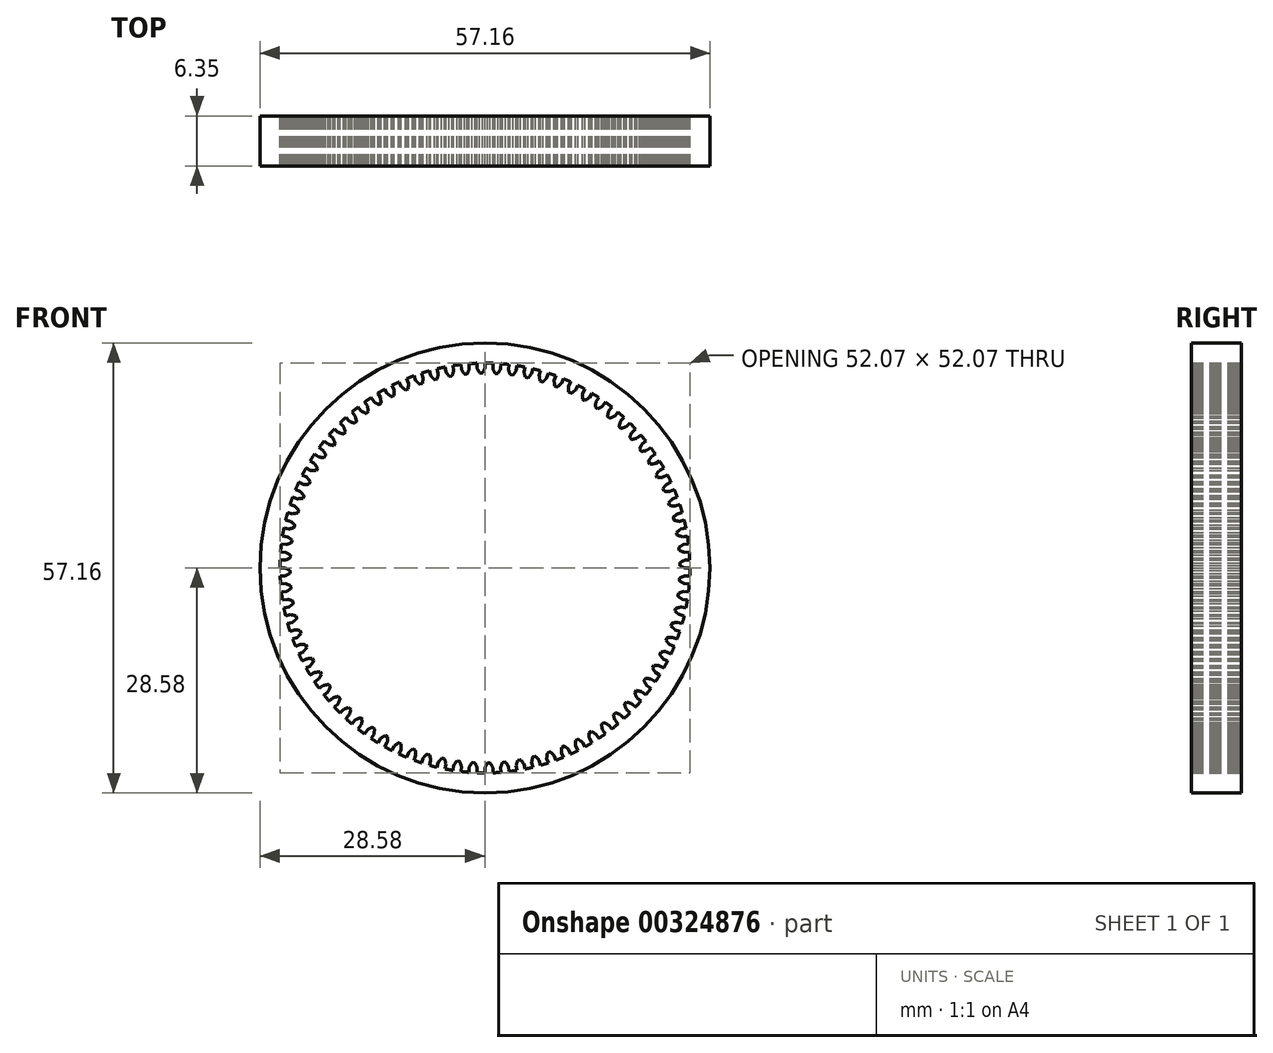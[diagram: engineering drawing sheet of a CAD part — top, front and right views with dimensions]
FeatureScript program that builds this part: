
annotation { "Feature Type Name" : "Feature", "Feature Type Description" : "" }
export const myFeature = defineFeature(function(context is Context, id is Id, definition is map)
    precondition{}
    {
        {
            var Q0;
            Q0=qCreatedBy(makeId("Front.planeOp"),FACE);
            var sketch = newSketch(context, id + "F0", { "sketchPlane" : qUnion([Q0])});
            skArc(sketch, "E0", {"start": v(-1.02, 26.01) * mm, "mid": v(-1.53, 25.99) * mm, "end": v(-2.04, 25.95) * mm});
            skArc(sketch, "E1.MirrorCS", {"start": v(0, 25.4) * mm, "mid": v(-0.14, 25.08) * mm, "end": v(-0.3, 24.77) * mm});
            skLineSegment(sketch, "E2.MirrorCS", {"start": v(0, 25.4) * mm, "end": v(0, 26.04) * mm});
            skLineSegment(sketch, "E3.MirrorCS", {"start": v(-1, 25.38) * mm, "end": v(-1.02, 26.01) * mm});
            skArc(sketch, "E4.MirrorCS", {"start": v(-1, 25.38) * mm, "mid": v(-0.84, 25.07) * mm, "end": v(-0.67, 24.76) * mm});
            skLineSegment(sketch, "E5", {"start": v(-0.67, 24.76) * mm, "end": v(-0.3, 24.77) * mm});
            skCircle(sketch, "E6", {"center": v(0, 0) * mm, "radius": 28.58 * mm});
            skLineSegment(sketch, "E7.1.0", {"start": v(-2, 25.32) * mm, "end": v(-2.04, 25.95) * mm});
            skLineSegment(sketch, "E7.1.1", {"start": v(-2.6, 24.63) * mm, "end": v(-2.25, 24.67) * mm});
            skArc(sketch, "E7.1.2", {"start": v(-2, 25.32) * mm, "mid": v(-2.11, 25) * mm, "end": v(-2.25, 24.67) * mm});
            skLineSegment(sketch, "E7.1.3", {"start": v(-2.99, 25.22) * mm, "end": v(-3.06, 25.85) * mm});
            skArc(sketch, "E7.1.4", {"start": v(-2.99, 25.22) * mm, "mid": v(-2.8, 24.92) * mm, "end": v(-2.6, 24.63) * mm});
            skArc(sketch, "E7.1.5", {"start": v(-2.99, 25.22) * mm, "mid": v(-2.8, 24.92) * mm, "end": v(-2.6, 24.63) * mm});
            skLineSegment(sketch, "E7.2.0", {"start": v(-3.97, 25.09) * mm, "end": v(-4.07, 25.71) * mm});
            skLineSegment(sketch, "E7.2.1", {"start": v(-4.53, 24.35) * mm, "end": v(-4.18, 24.41) * mm});
            skArc(sketch, "E7.2.2", {"start": v(-3.97, 25.09) * mm, "mid": v(-4.07, 24.75) * mm, "end": v(-4.18, 24.41) * mm});
            skLineSegment(sketch, "E7.2.3", {"start": v(-4.96, 24.91) * mm, "end": v(-5.08, 25.53) * mm});
            skArc(sketch, "E7.2.4", {"start": v(-4.96, 24.91) * mm, "mid": v(-4.75, 24.63) * mm, "end": v(-4.53, 24.35) * mm});
            skArc(sketch, "E7.2.5", {"start": v(-4.96, 24.91) * mm, "mid": v(-4.75, 24.63) * mm, "end": v(-4.53, 24.35) * mm});
            skLineSegment(sketch, "E8.3.3.0", {"start": v(-6.43, 23.92) * mm, "end": v(-6.08, 24.01) * mm});
            skArc(sketch, "E8.6.3.0", {"start": v(-5.93, 24.7) * mm, "mid": v(-6, 24.35) * mm, "end": v(-6.08, 24.01) * mm});
            skLineSegment(sketch, "E8.7.3.0", {"start": v(-5.93, 24.7) * mm, "end": v(-6.08, 25.32) * mm});
            skLineSegment(sketch, "E8.10.3.0", {"start": v(-6.9, 24.45) * mm, "end": v(-7.07, 25.06) * mm});
            skArc(sketch, "E8.13.3.0", {"start": v(-6.9, 24.45) * mm, "mid": v(-6.67, 24.18) * mm, "end": v(-6.43, 23.92) * mm});
            skArc(sketch, "E8.17.3.0", {"start": v(-6.9, 24.45) * mm, "mid": v(-6.67, 24.18) * mm, "end": v(-6.43, 23.92) * mm});
            skLineSegment(sketch, "E8.3.4.0", {"start": v(-8.28, 23.34) * mm, "end": v(-7.94, 23.46) * mm});
            skArc(sketch, "E8.6.4.0", {"start": v(-7.85, 24.16) * mm, "mid": v(-7.89, 23.8) * mm, "end": v(-7.94, 23.46) * mm});
            skLineSegment(sketch, "E8.7.4.0", {"start": v(-7.85, 24.16) * mm, "end": v(-8.05, 24.76) * mm});
            skLineSegment(sketch, "E8.10.4.0", {"start": v(-8.8, 23.83) * mm, "end": v(-9.01, 24.43) * mm});
            skArc(sketch, "E8.13.4.0", {"start": v(-8.8, 23.83) * mm, "mid": v(-8.54, 23.58) * mm, "end": v(-8.28, 23.34) * mm});
            skArc(sketch, "E8.17.4.0", {"start": v(-8.8, 23.83) * mm, "mid": v(-8.54, 23.58) * mm, "end": v(-8.28, 23.34) * mm});
            skLineSegment(sketch, "E8.3.5.0", {"start": v(-10.1, 22.62) * mm, "end": v(-9.76, 22.76) * mm});
            skArc(sketch, "E8.6.5.0", {"start": v(-9.72, 23.47) * mm, "mid": v(-9.73, 23.11) * mm, "end": v(-9.76, 22.76) * mm});
            skLineSegment(sketch, "E8.7.5.0", {"start": v(-9.72, 23.47) * mm, "end": v(-9.96, 24.05) * mm});
            skLineSegment(sketch, "E8.10.5.0", {"start": v(-10.63, 23.07) * mm, "end": v(-10.9, 23.64) * mm});
            skArc(sketch, "E8.13.5.0", {"start": v(-10.63, 23.07) * mm, "mid": v(-10.37, 22.84) * mm, "end": v(-10.1, 22.62) * mm});
            skArc(sketch, "E8.17.5.0", {"start": v(-10.63, 23.07) * mm, "mid": v(-10.37, 22.84) * mm, "end": v(-10.1, 22.62) * mm});
            skLineSegment(sketch, "E8.3.6.0", {"start": v(-11.83, 21.76) * mm, "end": v(-11.52, 21.93) * mm});
            skArc(sketch, "E8.6.6.0", {"start": v(-11.53, 22.63) * mm, "mid": v(-11.51, 22.28) * mm, "end": v(-11.52, 21.93) * mm});
            skLineSegment(sketch, "E8.7.6.0", {"start": v(-11.53, 22.63) * mm, "end": v(-11.82, 23.2) * mm});
            skLineSegment(sketch, "E8.10.6.0", {"start": v(-12.41, 22.16) * mm, "end": v(-12.72, 22.72) * mm});
            skArc(sketch, "E8.13.6.0", {"start": v(-12.41, 22.16) * mm, "mid": v(-12.13, 21.95) * mm, "end": v(-11.83, 21.76) * mm});
            skArc(sketch, "E8.17.6.0", {"start": v(-12.41, 22.16) * mm, "mid": v(-12.13, 21.95) * mm, "end": v(-11.83, 21.76) * mm});
            skLineSegment(sketch, "E8.3.7.0", {"start": v(-13.5, 20.76) * mm, "end": v(-13.2, 20.96) * mm});
            skArc(sketch, "E8.6.7.0", {"start": v(-13.27, 21.66) * mm, "mid": v(-13.23, 21.3) * mm, "end": v(-13.2, 20.96) * mm});
            skLineSegment(sketch, "E8.7.7.0", {"start": v(-13.27, 21.66) * mm, "end": v(-13.6, 22.2) * mm});
            skLineSegment(sketch, "E8.10.7.0", {"start": v(-14.11, 21.12) * mm, "end": v(-14.46, 21.65) * mm});
            skArc(sketch, "E8.13.7.0", {"start": v(-14.11, 21.12) * mm, "mid": v(-13.81, 20.93) * mm, "end": v(-13.5, 20.76) * mm});
            skArc(sketch, "E8.17.7.0", {"start": v(-14.11, 21.12) * mm, "mid": v(-13.81, 20.93) * mm, "end": v(-13.5, 20.76) * mm});
            skLineSegment(sketch, "E8.3.8.0", {"start": v(-15.1, 19.64) * mm, "end": v(-14.8, 19.86) * mm});
            skArc(sketch, "E8.6.8.0", {"start": v(-14.93, 20.55) * mm, "mid": v(-14.86, 20.2) * mm, "end": v(-14.8, 19.86) * mm});
            skLineSegment(sketch, "E8.7.8.0", {"start": v(-14.93, 20.55) * mm, "end": v(-15.3, 21.06) * mm});
            skLineSegment(sketch, "E8.10.8.0", {"start": v(-15.72, 19.95) * mm, "end": v(-16.12, 20.45) * mm});
            skArc(sketch, "E8.13.8.0", {"start": v(-15.72, 19.95) * mm, "mid": v(-15.41, 19.78) * mm, "end": v(-15.1, 19.64) * mm});
            skArc(sketch, "E8.17.8.0", {"start": v(-15.72, 19.95) * mm, "mid": v(-15.41, 19.78) * mm, "end": v(-15.1, 19.64) * mm});
            skLineSegment(sketch, "E8.3.9.0", {"start": v(-16.59, 18.4) * mm, "end": v(-16.32, 18.63) * mm});
            skArc(sketch, "E8.6.9.0", {"start": v(-16.5, 19.31) * mm, "mid": v(-16.4, 18.98) * mm, "end": v(-16.32, 18.63) * mm});
            skLineSegment(sketch, "E8.7.9.0", {"start": v(-16.5, 19.31) * mm, "end": v(-16.9, 19.8) * mm});
            skLineSegment(sketch, "E8.10.9.0", {"start": v(-17.24, 18.65) * mm, "end": v(-17.67, 19.12) * mm});
            skArc(sketch, "E8.13.9.0", {"start": v(-17.24, 18.65) * mm, "mid": v(-16.92, 18.51) * mm, "end": v(-16.59, 18.4) * mm});
            skArc(sketch, "E8.17.9.0", {"start": v(-17.24, 18.65) * mm, "mid": v(-16.92, 18.51) * mm, "end": v(-16.59, 18.4) * mm});
            skLineSegment(sketch, "E8.3.10.0", {"start": v(-17.98, 17.04) * mm, "end": v(-17.73, 17.3) * mm});
            skArc(sketch, "E8.6.10.0", {"start": v(-17.96, 17.96) * mm, "mid": v(-17.84, 17.63) * mm, "end": v(-17.73, 17.3) * mm});
            skLineSegment(sketch, "E8.7.10.0", {"start": v(-17.96, 17.96) * mm, "end": v(-18.4, 18.4) * mm});
            skLineSegment(sketch, "E8.10.10.0", {"start": v(-18.65, 17.24) * mm, "end": v(-19.12, 17.67) * mm});
            skArc(sketch, "E8.13.10.0", {"start": v(-18.65, 17.24) * mm, "mid": v(-18.32, 17.13) * mm, "end": v(-17.98, 17.04) * mm});
            skArc(sketch, "E8.17.10.0", {"start": v(-18.65, 17.24) * mm, "mid": v(-18.32, 17.13) * mm, "end": v(-17.98, 17.04) * mm});
            skLineSegment(sketch, "E8.3.11.0", {"start": v(-19.26, 15.57) * mm, "end": v(-19.03, 15.85) * mm});
            skArc(sketch, "E8.6.11.0", {"start": v(-19.31, 16.5) * mm, "mid": v(-19.16, 16.18) * mm, "end": v(-19.03, 15.85) * mm});
            skLineSegment(sketch, "E8.7.11.0", {"start": v(-19.31, 16.5) * mm, "end": v(-19.8, 16.9) * mm});
            skLineSegment(sketch, "E8.10.11.0", {"start": v(-19.95, 15.72) * mm, "end": v(-20.45, 16.12) * mm});
            skArc(sketch, "E8.13.11.0", {"start": v(-19.95, 15.72) * mm, "mid": v(-19.6, 15.64) * mm, "end": v(-19.26, 15.57) * mm});
            skArc(sketch, "E8.17.11.0", {"start": v(-19.95, 15.72) * mm, "mid": v(-19.6, 15.64) * mm, "end": v(-19.26, 15.57) * mm});
            skLineSegment(sketch, "E8.3.12.0", {"start": v(-20.42, 14.01) * mm, "end": v(-20.22, 14.3) * mm});
            skArc(sketch, "E8.6.12.0", {"start": v(-20.55, 14.93) * mm, "mid": v(-20.37, 14.62) * mm, "end": v(-20.22, 14.3) * mm});
            skLineSegment(sketch, "E8.7.12.0", {"start": v(-20.55, 14.93) * mm, "end": v(-21.06, 15.3) * mm});
            skLineSegment(sketch, "E8.10.12.0", {"start": v(-21.12, 14.11) * mm, "end": v(-21.65, 14.46) * mm});
            skArc(sketch, "E8.13.12.0", {"start": v(-21.12, 14.11) * mm, "mid": v(-20.77, 14.05) * mm, "end": v(-20.42, 14.01) * mm});
            skArc(sketch, "E8.17.12.0", {"start": v(-21.12, 14.11) * mm, "mid": v(-20.77, 14.05) * mm, "end": v(-20.42, 14.01) * mm});
            skLineSegment(sketch, "E8.3.13.0", {"start": v(-21.46, 12.37) * mm, "end": v(-21.28, 12.68) * mm});
            skArc(sketch, "E8.6.13.0", {"start": v(-21.66, 13.27) * mm, "mid": v(-21.46, 12.98) * mm, "end": v(-21.28, 12.68) * mm});
            skLineSegment(sketch, "E8.7.13.0", {"start": v(-21.66, 13.27) * mm, "end": v(-22.2, 13.6) * mm});
            skLineSegment(sketch, "E8.10.13.0", {"start": v(-22.16, 12.41) * mm, "end": v(-22.72, 12.72) * mm});
            skArc(sketch, "E8.13.13.0", {"start": v(-22.16, 12.41) * mm, "mid": v(-21.81, 12.38) * mm, "end": v(-21.46, 12.37) * mm});
            skArc(sketch, "E8.17.13.0", {"start": v(-22.16, 12.41) * mm, "mid": v(-21.81, 12.38) * mm, "end": v(-21.46, 12.37) * mm});
            skLineSegment(sketch, "E8.3.14.0", {"start": v(-22.36, 10.65) * mm, "end": v(-22.2, 10.97) * mm});
            skArc(sketch, "E8.6.14.0", {"start": v(-22.63, 11.53) * mm, "mid": v(-22.41, 11.26) * mm, "end": v(-22.2, 10.97) * mm});
            skLineSegment(sketch, "E8.7.14.0", {"start": v(-22.63, 11.53) * mm, "end": v(-23.2, 11.82) * mm});
            skLineSegment(sketch, "E8.10.14.0", {"start": v(-23.07, 10.63) * mm, "end": v(-23.64, 10.9) * mm});
            skArc(sketch, "E8.13.14.0", {"start": v(-23.07, 10.63) * mm, "mid": v(-22.72, 10.63) * mm, "end": v(-22.36, 10.65) * mm});
            skArc(sketch, "E8.17.14.0", {"start": v(-23.07, 10.63) * mm, "mid": v(-22.72, 10.63) * mm, "end": v(-22.36, 10.65) * mm});
            skLineSegment(sketch, "E8.3.15.0", {"start": v(-23.13, 8.86) * mm, "end": v(-23, 9.2) * mm});
            skArc(sketch, "E8.6.15.0", {"start": v(-23.47, 9.72) * mm, "mid": v(-23.23, 9.46) * mm, "end": v(-23, 9.2) * mm});
            skLineSegment(sketch, "E8.7.15.0", {"start": v(-23.47, 9.72) * mm, "end": v(-24.05, 9.96) * mm});
            skLineSegment(sketch, "E8.10.15.0", {"start": v(-23.83, 8.8) * mm, "end": v(-24.43, 9.01) * mm});
            skArc(sketch, "E8.13.15.0", {"start": v(-23.83, 8.8) * mm, "mid": v(-23.48, 8.82) * mm, "end": v(-23.13, 8.86) * mm});
            skArc(sketch, "E8.17.15.0", {"start": v(-23.83, 8.8) * mm, "mid": v(-23.48, 8.82) * mm, "end": v(-23.13, 8.86) * mm});
            skLineSegment(sketch, "E8.3.16.0", {"start": v(-23.75, 7.02) * mm, "end": v(-23.65, 7.36) * mm});
            skArc(sketch, "E8.6.16.0", {"start": v(-24.16, 7.85) * mm, "mid": v(-23.9, 7.61) * mm, "end": v(-23.65, 7.36) * mm});
            skLineSegment(sketch, "E8.7.16.0", {"start": v(-24.16, 7.85) * mm, "end": v(-24.76, 8.05) * mm});
            skLineSegment(sketch, "E8.10.16.0", {"start": v(-24.45, 6.9) * mm, "end": v(-25.06, 7.07) * mm});
            skArc(sketch, "E8.13.16.0", {"start": v(-24.45, 6.9) * mm, "mid": v(-24.1, 6.95) * mm, "end": v(-23.75, 7.02) * mm});
            skArc(sketch, "E8.17.16.0", {"start": v(-24.45, 6.9) * mm, "mid": v(-24.1, 6.95) * mm, "end": v(-23.75, 7.02) * mm});
            skLineSegment(sketch, "E8.3.17.0", {"start": v(-24.23, 5.13) * mm, "end": v(-24.15, 5.48) * mm});
            skArc(sketch, "E8.6.17.0", {"start": v(-24.7, 5.93) * mm, "mid": v(-24.42, 5.71) * mm, "end": v(-24.15, 5.48) * mm});
            skLineSegment(sketch, "E8.7.17.0", {"start": v(-24.7, 5.93) * mm, "end": v(-25.32, 6.08) * mm});
            skLineSegment(sketch, "E8.10.17.0", {"start": v(-24.91, 4.96) * mm, "end": v(-25.53, 5.08) * mm});
            skArc(sketch, "E8.13.17.0", {"start": v(-24.91, 4.96) * mm, "mid": v(-24.57, 5.03) * mm, "end": v(-24.23, 5.13) * mm});
            skArc(sketch, "E8.17.17.0", {"start": v(-24.91, 4.96) * mm, "mid": v(-24.57, 5.03) * mm, "end": v(-24.23, 5.13) * mm});
            skLineSegment(sketch, "E8.3.18.0", {"start": v(-24.56, 3.22) * mm, "end": v(-24.5, 3.57) * mm});
            skArc(sketch, "E8.6.18.0", {"start": v(-25.09, 3.97) * mm, "mid": v(-24.8, 3.78) * mm, "end": v(-24.5, 3.57) * mm});
            skLineSegment(sketch, "E8.7.18.0", {"start": v(-25.09, 3.97) * mm, "end": v(-25.71, 4.07) * mm});
            skLineSegment(sketch, "E8.10.18.0", {"start": v(-25.22, 2.99) * mm, "end": v(-25.85, 3.06) * mm});
            skArc(sketch, "E8.13.18.0", {"start": v(-25.22, 2.99) * mm, "mid": v(-24.89, 3.1) * mm, "end": v(-24.56, 3.22) * mm});
            skArc(sketch, "E8.17.18.0", {"start": v(-25.22, 2.99) * mm, "mid": v(-24.89, 3.1) * mm, "end": v(-24.56, 3.22) * mm});
            skLineSegment(sketch, "E8.3.19.0", {"start": v(-24.74, 1.28) * mm, "end": v(-24.71, 1.64) * mm});
            skArc(sketch, "E8.6.19.0", {"start": v(-25.32, 2) * mm, "mid": v(-25.01, 1.82) * mm, "end": v(-24.71, 1.64) * mm});
            skLineSegment(sketch, "E8.7.19.0", {"start": v(-25.32, 2) * mm, "end": v(-25.95, 2.04) * mm});
            skLineSegment(sketch, "E8.10.19.0", {"start": v(-25.38, 1) * mm, "end": v(-26.01, 1.02) * mm});
            skArc(sketch, "E8.13.19.0", {"start": v(-25.38, 1) * mm, "mid": v(-25.05, 1.13) * mm, "end": v(-24.74, 1.28) * mm});
            skArc(sketch, "E8.17.19.0", {"start": v(-25.38, 1) * mm, "mid": v(-25.05, 1.13) * mm, "end": v(-24.74, 1.28) * mm});
            skLineSegment(sketch, "E8.3.20.0", {"start": v(-24.76, -0.67) * mm, "end": v(-24.77, -0.3) * mm});
            skArc(sketch, "E8.6.20.0", {"start": v(-25.4, 0) * mm, "mid": v(-25.08, -0.14) * mm, "end": v(-24.77, -0.3) * mm});
            skLineSegment(sketch, "E8.7.20.0", {"start": v(-25.4, 0) * mm, "end": v(-26.04, 0) * mm});
            skLineSegment(sketch, "E8.10.20.0", {"start": v(-25.38, -1) * mm, "end": v(-26.01, -1.02) * mm});
            skArc(sketch, "E8.13.20.0", {"start": v(-25.38, -1) * mm, "mid": v(-25.07, -0.84) * mm, "end": v(-24.76, -0.67) * mm});
            skArc(sketch, "E8.17.20.0", {"start": v(-25.38, -1) * mm, "mid": v(-25.07, -0.84) * mm, "end": v(-24.76, -0.67) * mm});
            skLineSegment(sketch, "E8.3.21.0", {"start": v(-24.63, -2.6) * mm, "end": v(-24.67, -2.25) * mm});
            skArc(sketch, "E8.6.21.0", {"start": v(-25.32, -2) * mm, "mid": v(-25, -2.11) * mm, "end": v(-24.67, -2.25) * mm});
            skLineSegment(sketch, "E8.7.21.0", {"start": v(-25.32, -2) * mm, "end": v(-25.95, -2.04) * mm});
            skLineSegment(sketch, "E8.10.21.0", {"start": v(-25.22, -2.99) * mm, "end": v(-25.85, -3.06) * mm});
            skArc(sketch, "E8.13.21.0", {"start": v(-25.22, -2.99) * mm, "mid": v(-24.92, -2.8) * mm, "end": v(-24.63, -2.6) * mm});
            skArc(sketch, "E8.17.21.0", {"start": v(-25.22, -2.99) * mm, "mid": v(-24.92, -2.8) * mm, "end": v(-24.63, -2.6) * mm});
            skLineSegment(sketch, "E8.3.22.0", {"start": v(-24.35, -4.53) * mm, "end": v(-24.41, -4.18) * mm});
            skArc(sketch, "E8.6.22.0", {"start": v(-25.09, -3.97) * mm, "mid": v(-24.75, -4.07) * mm, "end": v(-24.41, -4.18) * mm});
            skLineSegment(sketch, "E8.7.22.0", {"start": v(-25.09, -3.97) * mm, "end": v(-25.71, -4.07) * mm});
            skLineSegment(sketch, "E8.10.22.0", {"start": v(-24.91, -4.96) * mm, "end": v(-25.53, -5.08) * mm});
            skArc(sketch, "E8.13.22.0", {"start": v(-24.91, -4.96) * mm, "mid": v(-24.63, -4.75) * mm, "end": v(-24.35, -4.53) * mm});
            skArc(sketch, "E8.17.22.0", {"start": v(-24.91, -4.96) * mm, "mid": v(-24.63, -4.75) * mm, "end": v(-24.35, -4.53) * mm});
            skLineSegment(sketch, "E8.3.23.0", {"start": v(-23.92, -6.43) * mm, "end": v(-24.01, -6.08) * mm});
            skArc(sketch, "E8.6.23.0", {"start": v(-24.7, -5.93) * mm, "mid": v(-24.35, -6) * mm, "end": v(-24.01, -6.08) * mm});
            skLineSegment(sketch, "E8.7.23.0", {"start": v(-24.7, -5.93) * mm, "end": v(-25.32, -6.08) * mm});
            skLineSegment(sketch, "E8.10.23.0", {"start": v(-24.45, -6.9) * mm, "end": v(-25.06, -7.07) * mm});
            skArc(sketch, "E8.13.23.0", {"start": v(-24.45, -6.9) * mm, "mid": v(-24.18, -6.67) * mm, "end": v(-23.92, -6.43) * mm});
            skArc(sketch, "E8.17.23.0", {"start": v(-24.45, -6.9) * mm, "mid": v(-24.18, -6.67) * mm, "end": v(-23.92, -6.43) * mm});
            skLineSegment(sketch, "E8.3.24.0", {"start": v(-23.34, -8.28) * mm, "end": v(-23.46, -7.94) * mm});
            skArc(sketch, "E8.6.24.0", {"start": v(-24.16, -7.85) * mm, "mid": v(-23.8, -7.89) * mm, "end": v(-23.46, -7.94) * mm});
            skLineSegment(sketch, "E8.7.24.0", {"start": v(-24.16, -7.85) * mm, "end": v(-24.76, -8.05) * mm});
            skLineSegment(sketch, "E8.10.24.0", {"start": v(-23.83, -8.8) * mm, "end": v(-24.43, -9.01) * mm});
            skArc(sketch, "E8.13.24.0", {"start": v(-23.83, -8.8) * mm, "mid": v(-23.58, -8.54) * mm, "end": v(-23.34, -8.28) * mm});
            skArc(sketch, "E8.17.24.0", {"start": v(-23.83, -8.8) * mm, "mid": v(-23.58, -8.54) * mm, "end": v(-23.34, -8.28) * mm});
            skLineSegment(sketch, "E8.3.25.0", {"start": v(-22.62, -10.1) * mm, "end": v(-22.76, -9.76) * mm});
            skArc(sketch, "E8.6.25.0", {"start": v(-23.47, -9.72) * mm, "mid": v(-23.11, -9.73) * mm, "end": v(-22.76, -9.76) * mm});
            skLineSegment(sketch, "E8.7.25.0", {"start": v(-23.47, -9.72) * mm, "end": v(-24.05, -9.96) * mm});
            skLineSegment(sketch, "E8.10.25.0", {"start": v(-23.07, -10.63) * mm, "end": v(-23.64, -10.9) * mm});
            skArc(sketch, "E8.13.25.0", {"start": v(-23.07, -10.63) * mm, "mid": v(-22.84, -10.37) * mm, "end": v(-22.62, -10.1) * mm});
            skArc(sketch, "E8.17.25.0", {"start": v(-23.07, -10.63) * mm, "mid": v(-22.84, -10.37) * mm, "end": v(-22.62, -10.1) * mm});
            skLineSegment(sketch, "E8.3.26.0", {"start": v(-21.76, -11.83) * mm, "end": v(-21.93, -11.52) * mm});
            skArc(sketch, "E8.6.26.0", {"start": v(-22.63, -11.53) * mm, "mid": v(-22.28, -11.51) * mm, "end": v(-21.93, -11.52) * mm});
            skLineSegment(sketch, "E8.7.26.0", {"start": v(-22.63, -11.53) * mm, "end": v(-23.2, -11.82) * mm});
            skLineSegment(sketch, "E8.10.26.0", {"start": v(-22.16, -12.41) * mm, "end": v(-22.72, -12.72) * mm});
            skArc(sketch, "E8.13.26.0", {"start": v(-22.16, -12.41) * mm, "mid": v(-21.95, -12.13) * mm, "end": v(-21.76, -11.83) * mm});
            skArc(sketch, "E8.17.26.0", {"start": v(-22.16, -12.41) * mm, "mid": v(-21.95, -12.13) * mm, "end": v(-21.76, -11.83) * mm});
            skLineSegment(sketch, "E8.3.27.0", {"start": v(-20.76, -13.5) * mm, "end": v(-20.96, -13.2) * mm});
            skArc(sketch, "E8.6.27.0", {"start": v(-21.66, -13.27) * mm, "mid": v(-21.3, -13.23) * mm, "end": v(-20.96, -13.2) * mm});
            skLineSegment(sketch, "E8.7.27.0", {"start": v(-21.66, -13.27) * mm, "end": v(-22.2, -13.6) * mm});
            skLineSegment(sketch, "E8.10.27.0", {"start": v(-21.12, -14.11) * mm, "end": v(-21.65, -14.46) * mm});
            skArc(sketch, "E8.13.27.0", {"start": v(-21.12, -14.11) * mm, "mid": v(-20.93, -13.81) * mm, "end": v(-20.76, -13.5) * mm});
            skArc(sketch, "E8.17.27.0", {"start": v(-21.12, -14.11) * mm, "mid": v(-20.93, -13.81) * mm, "end": v(-20.76, -13.5) * mm});
            skLineSegment(sketch, "E8.3.28.0", {"start": v(-19.64, -15.1) * mm, "end": v(-19.86, -14.8) * mm});
            skArc(sketch, "E8.6.28.0", {"start": v(-20.55, -14.93) * mm, "mid": v(-20.2, -14.86) * mm, "end": v(-19.86, -14.8) * mm});
            skLineSegment(sketch, "E8.7.28.0", {"start": v(-20.55, -14.93) * mm, "end": v(-21.06, -15.3) * mm});
            skLineSegment(sketch, "E8.10.28.0", {"start": v(-19.95, -15.72) * mm, "end": v(-20.45, -16.12) * mm});
            skArc(sketch, "E8.13.28.0", {"start": v(-19.95, -15.72) * mm, "mid": v(-19.78, -15.41) * mm, "end": v(-19.64, -15.1) * mm});
            skArc(sketch, "E8.17.28.0", {"start": v(-19.95, -15.72) * mm, "mid": v(-19.78, -15.41) * mm, "end": v(-19.64, -15.1) * mm});
            skLineSegment(sketch, "E8.3.29.0", {"start": v(-18.4, -16.59) * mm, "end": v(-18.63, -16.32) * mm});
            skArc(sketch, "E8.6.29.0", {"start": v(-19.31, -16.5) * mm, "mid": v(-18.98, -16.4) * mm, "end": v(-18.63, -16.32) * mm});
            skLineSegment(sketch, "E8.7.29.0", {"start": v(-19.31, -16.5) * mm, "end": v(-19.8, -16.9) * mm});
            skLineSegment(sketch, "E8.10.29.0", {"start": v(-18.65, -17.24) * mm, "end": v(-19.12, -17.67) * mm});
            skArc(sketch, "E8.13.29.0", {"start": v(-18.65, -17.24) * mm, "mid": v(-18.51, -16.92) * mm, "end": v(-18.4, -16.59) * mm});
            skArc(sketch, "E8.17.29.0", {"start": v(-18.65, -17.24) * mm, "mid": v(-18.51, -16.92) * mm, "end": v(-18.4, -16.59) * mm});
            skLineSegment(sketch, "E8.3.30.0", {"start": v(-17.04, -17.98) * mm, "end": v(-17.3, -17.73) * mm});
            skArc(sketch, "E8.6.30.0", {"start": v(-17.96, -17.96) * mm, "mid": v(-17.63, -17.84) * mm, "end": v(-17.3, -17.73) * mm});
            skLineSegment(sketch, "E8.7.30.0", {"start": v(-17.96, -17.96) * mm, "end": v(-18.4, -18.4) * mm});
            skLineSegment(sketch, "E8.10.30.0", {"start": v(-17.24, -18.65) * mm, "end": v(-17.67, -19.12) * mm});
            skArc(sketch, "E8.13.30.0", {"start": v(-17.24, -18.65) * mm, "mid": v(-17.13, -18.32) * mm, "end": v(-17.04, -17.98) * mm});
            skArc(sketch, "E8.17.30.0", {"start": v(-17.24, -18.65) * mm, "mid": v(-17.13, -18.32) * mm, "end": v(-17.04, -17.98) * mm});
            skLineSegment(sketch, "E8.3.31.0", {"start": v(-15.57, -19.26) * mm, "end": v(-15.85, -19.03) * mm});
            skArc(sketch, "E8.6.31.0", {"start": v(-16.5, -19.31) * mm, "mid": v(-16.18, -19.16) * mm, "end": v(-15.85, -19.03) * mm});
            skLineSegment(sketch, "E8.7.31.0", {"start": v(-16.5, -19.31) * mm, "end": v(-16.9, -19.8) * mm});
            skLineSegment(sketch, "E8.10.31.0", {"start": v(-15.72, -19.95) * mm, "end": v(-16.12, -20.45) * mm});
            skArc(sketch, "E8.13.31.0", {"start": v(-15.72, -19.95) * mm, "mid": v(-15.64, -19.6) * mm, "end": v(-15.57, -19.26) * mm});
            skArc(sketch, "E8.17.31.0", {"start": v(-15.72, -19.95) * mm, "mid": v(-15.64, -19.6) * mm, "end": v(-15.57, -19.26) * mm});
            skLineSegment(sketch, "E8.3.32.0", {"start": v(-14.01, -20.42) * mm, "end": v(-14.3, -20.22) * mm});
            skArc(sketch, "E8.6.32.0", {"start": v(-14.93, -20.55) * mm, "mid": v(-14.62, -20.37) * mm, "end": v(-14.3, -20.22) * mm});
            skLineSegment(sketch, "E8.7.32.0", {"start": v(-14.93, -20.55) * mm, "end": v(-15.3, -21.06) * mm});
            skLineSegment(sketch, "E8.10.32.0", {"start": v(-14.11, -21.12) * mm, "end": v(-14.46, -21.65) * mm});
            skArc(sketch, "E8.13.32.0", {"start": v(-14.11, -21.12) * mm, "mid": v(-14.05, -20.77) * mm, "end": v(-14.01, -20.42) * mm});
            skArc(sketch, "E8.17.32.0", {"start": v(-14.11, -21.12) * mm, "mid": v(-14.05, -20.77) * mm, "end": v(-14.01, -20.42) * mm});
            skLineSegment(sketch, "E8.3.33.0", {"start": v(-12.37, -21.46) * mm, "end": v(-12.68, -21.28) * mm});
            skArc(sketch, "E8.6.33.0", {"start": v(-13.27, -21.66) * mm, "mid": v(-12.98, -21.46) * mm, "end": v(-12.68, -21.28) * mm});
            skLineSegment(sketch, "E8.7.33.0", {"start": v(-13.27, -21.66) * mm, "end": v(-13.6, -22.2) * mm});
            skLineSegment(sketch, "E8.10.33.0", {"start": v(-12.41, -22.16) * mm, "end": v(-12.72, -22.72) * mm});
            skArc(sketch, "E8.13.33.0", {"start": v(-12.41, -22.16) * mm, "mid": v(-12.38, -21.81) * mm, "end": v(-12.37, -21.46) * mm});
            skArc(sketch, "E8.17.33.0", {"start": v(-12.41, -22.16) * mm, "mid": v(-12.38, -21.81) * mm, "end": v(-12.37, -21.46) * mm});
            skLineSegment(sketch, "E8.3.34.0", {"start": v(-10.65, -22.36) * mm, "end": v(-10.97, -22.2) * mm});
            skArc(sketch, "E8.6.34.0", {"start": v(-11.53, -22.63) * mm, "mid": v(-11.26, -22.41) * mm, "end": v(-10.97, -22.2) * mm});
            skLineSegment(sketch, "E8.7.34.0", {"start": v(-11.53, -22.63) * mm, "end": v(-11.82, -23.2) * mm});
            skLineSegment(sketch, "E8.10.34.0", {"start": v(-10.63, -23.07) * mm, "end": v(-10.9, -23.64) * mm});
            skArc(sketch, "E8.13.34.0", {"start": v(-10.63, -23.07) * mm, "mid": v(-10.63, -22.72) * mm, "end": v(-10.65, -22.36) * mm});
            skArc(sketch, "E8.17.34.0", {"start": v(-10.63, -23.07) * mm, "mid": v(-10.63, -22.72) * mm, "end": v(-10.65, -22.36) * mm});
            skLineSegment(sketch, "E8.3.35.0", {"start": v(-8.86, -23.13) * mm, "end": v(-9.2, -23) * mm});
            skArc(sketch, "E8.6.35.0", {"start": v(-9.72, -23.47) * mm, "mid": v(-9.46, -23.23) * mm, "end": v(-9.2, -23) * mm});
            skLineSegment(sketch, "E8.7.35.0", {"start": v(-9.72, -23.47) * mm, "end": v(-9.96, -24.05) * mm});
            skLineSegment(sketch, "E8.10.35.0", {"start": v(-8.8, -23.83) * mm, "end": v(-9.01, -24.43) * mm});
            skArc(sketch, "E8.13.35.0", {"start": v(-8.8, -23.83) * mm, "mid": v(-8.82, -23.48) * mm, "end": v(-8.86, -23.13) * mm});
            skArc(sketch, "E8.17.35.0", {"start": v(-8.8, -23.83) * mm, "mid": v(-8.82, -23.48) * mm, "end": v(-8.86, -23.13) * mm});
            skLineSegment(sketch, "E8.3.36.0", {"start": v(-7.02, -23.75) * mm, "end": v(-7.36, -23.65) * mm});
            skArc(sketch, "E8.6.36.0", {"start": v(-7.85, -24.16) * mm, "mid": v(-7.61, -23.9) * mm, "end": v(-7.36, -23.65) * mm});
            skLineSegment(sketch, "E8.7.36.0", {"start": v(-7.85, -24.16) * mm, "end": v(-8.05, -24.76) * mm});
            skLineSegment(sketch, "E8.10.36.0", {"start": v(-6.9, -24.45) * mm, "end": v(-7.07, -25.06) * mm});
            skArc(sketch, "E8.13.36.0", {"start": v(-6.9, -24.45) * mm, "mid": v(-6.95, -24.1) * mm, "end": v(-7.02, -23.75) * mm});
            skArc(sketch, "E8.17.36.0", {"start": v(-6.9, -24.45) * mm, "mid": v(-6.95, -24.1) * mm, "end": v(-7.02, -23.75) * mm});
            skLineSegment(sketch, "E8.3.37.0", {"start": v(-5.13, -24.23) * mm, "end": v(-5.48, -24.15) * mm});
            skArc(sketch, "E8.6.37.0", {"start": v(-5.93, -24.7) * mm, "mid": v(-5.71, -24.42) * mm, "end": v(-5.48, -24.15) * mm});
            skLineSegment(sketch, "E8.7.37.0", {"start": v(-5.93, -24.7) * mm, "end": v(-6.08, -25.32) * mm});
            skLineSegment(sketch, "E8.10.37.0", {"start": v(-4.96, -24.91) * mm, "end": v(-5.08, -25.53) * mm});
            skArc(sketch, "E8.13.37.0", {"start": v(-4.96, -24.91) * mm, "mid": v(-5.03, -24.57) * mm, "end": v(-5.13, -24.23) * mm});
            skArc(sketch, "E8.17.37.0", {"start": v(-4.96, -24.91) * mm, "mid": v(-5.03, -24.57) * mm, "end": v(-5.13, -24.23) * mm});
            skLineSegment(sketch, "E8.3.38.0", {"start": v(-3.22, -24.56) * mm, "end": v(-3.57, -24.5) * mm});
            skArc(sketch, "E8.6.38.0", {"start": v(-3.97, -25.09) * mm, "mid": v(-3.78, -24.8) * mm, "end": v(-3.57, -24.5) * mm});
            skLineSegment(sketch, "E8.7.38.0", {"start": v(-3.97, -25.09) * mm, "end": v(-4.07, -25.71) * mm});
            skLineSegment(sketch, "E8.10.38.0", {"start": v(-2.99, -25.22) * mm, "end": v(-3.06, -25.85) * mm});
            skArc(sketch, "E8.13.38.0", {"start": v(-2.99, -25.22) * mm, "mid": v(-3.1, -24.89) * mm, "end": v(-3.22, -24.56) * mm});
            skArc(sketch, "E8.17.38.0", {"start": v(-2.99, -25.22) * mm, "mid": v(-3.1, -24.89) * mm, "end": v(-3.22, -24.56) * mm});
            skLineSegment(sketch, "E8.3.39.0", {"start": v(-1.28, -24.74) * mm, "end": v(-1.64, -24.71) * mm});
            skArc(sketch, "E8.6.39.0", {"start": v(-2, -25.32) * mm, "mid": v(-1.82, -25.01) * mm, "end": v(-1.64, -24.71) * mm});
            skLineSegment(sketch, "E8.7.39.0", {"start": v(-2, -25.32) * mm, "end": v(-2.04, -25.95) * mm});
            skLineSegment(sketch, "E8.10.39.0", {"start": v(-1, -25.38) * mm, "end": v(-1.02, -26.01) * mm});
            skArc(sketch, "E8.13.39.0", {"start": v(-1, -25.38) * mm, "mid": v(-1.13, -25.05) * mm, "end": v(-1.28, -24.74) * mm});
            skArc(sketch, "E8.17.39.0", {"start": v(-1, -25.38) * mm, "mid": v(-1.13, -25.05) * mm, "end": v(-1.28, -24.74) * mm});
            skLineSegment(sketch, "E8.3.40.0", {"start": v(0.67, -24.76) * mm, "end": v(0.3, -24.77) * mm});
            skArc(sketch, "E8.6.40.0", {"start": v(0, -25.4) * mm, "mid": v(0.14, -25.08) * mm, "end": v(0.3, -24.77) * mm});
            skLineSegment(sketch, "E8.7.40.0", {"start": v(0, -25.4) * mm, "end": v(0, -26.04) * mm});
            skLineSegment(sketch, "E8.10.40.0", {"start": v(1, -25.38) * mm, "end": v(1.02, -26.01) * mm});
            skArc(sketch, "E8.13.40.0", {"start": v(1, -25.38) * mm, "mid": v(0.84, -25.07) * mm, "end": v(0.67, -24.76) * mm});
            skArc(sketch, "E8.17.40.0", {"start": v(1, -25.38) * mm, "mid": v(0.84, -25.07) * mm, "end": v(0.67, -24.76) * mm});
            skLineSegment(sketch, "E8.3.41.0", {"start": v(2.6, -24.63) * mm, "end": v(2.25, -24.67) * mm});
            skArc(sketch, "E8.6.41.0", {"start": v(2, -25.32) * mm, "mid": v(2.11, -25) * mm, "end": v(2.25, -24.67) * mm});
            skLineSegment(sketch, "E8.7.41.0", {"start": v(2, -25.32) * mm, "end": v(2.04, -25.95) * mm});
            skLineSegment(sketch, "E8.10.41.0", {"start": v(2.99, -25.22) * mm, "end": v(3.06, -25.85) * mm});
            skArc(sketch, "E8.13.41.0", {"start": v(2.99, -25.22) * mm, "mid": v(2.8, -24.92) * mm, "end": v(2.6, -24.63) * mm});
            skArc(sketch, "E8.17.41.0", {"start": v(2.99, -25.22) * mm, "mid": v(2.8, -24.92) * mm, "end": v(2.6, -24.63) * mm});
            skLineSegment(sketch, "E8.3.42.0", {"start": v(4.53, -24.35) * mm, "end": v(4.18, -24.41) * mm});
            skArc(sketch, "E8.6.42.0", {"start": v(3.97, -25.09) * mm, "mid": v(4.07, -24.75) * mm, "end": v(4.18, -24.41) * mm});
            skLineSegment(sketch, "E8.7.42.0", {"start": v(3.97, -25.09) * mm, "end": v(4.07, -25.71) * mm});
            skLineSegment(sketch, "E8.10.42.0", {"start": v(4.96, -24.91) * mm, "end": v(5.08, -25.53) * mm});
            skArc(sketch, "E8.13.42.0", {"start": v(4.96, -24.91) * mm, "mid": v(4.75, -24.63) * mm, "end": v(4.53, -24.35) * mm});
            skArc(sketch, "E8.17.42.0", {"start": v(4.96, -24.91) * mm, "mid": v(4.75, -24.63) * mm, "end": v(4.53, -24.35) * mm});
            skLineSegment(sketch, "E8.3.43.0", {"start": v(6.43, -23.92) * mm, "end": v(6.08, -24.01) * mm});
            skArc(sketch, "E8.6.43.0", {"start": v(5.93, -24.7) * mm, "mid": v(6, -24.35) * mm, "end": v(6.08, -24.01) * mm});
            skLineSegment(sketch, "E8.7.43.0", {"start": v(5.93, -24.7) * mm, "end": v(6.08, -25.32) * mm});
            skLineSegment(sketch, "E8.10.43.0", {"start": v(6.9, -24.45) * mm, "end": v(7.07, -25.06) * mm});
            skArc(sketch, "E8.13.43.0", {"start": v(6.9, -24.45) * mm, "mid": v(6.67, -24.18) * mm, "end": v(6.43, -23.92) * mm});
            skArc(sketch, "E8.17.43.0", {"start": v(6.9, -24.45) * mm, "mid": v(6.67, -24.18) * mm, "end": v(6.43, -23.92) * mm});
            skLineSegment(sketch, "E8.3.44.0", {"start": v(8.28, -23.34) * mm, "end": v(7.94, -23.46) * mm});
            skArc(sketch, "E8.6.44.0", {"start": v(7.85, -24.16) * mm, "mid": v(7.89, -23.8) * mm, "end": v(7.94, -23.46) * mm});
            skLineSegment(sketch, "E8.7.44.0", {"start": v(7.85, -24.16) * mm, "end": v(8.05, -24.76) * mm});
            skLineSegment(sketch, "E8.10.44.0", {"start": v(8.8, -23.83) * mm, "end": v(9.01, -24.43) * mm});
            skArc(sketch, "E8.13.44.0", {"start": v(8.8, -23.83) * mm, "mid": v(8.54, -23.58) * mm, "end": v(8.28, -23.34) * mm});
            skArc(sketch, "E8.17.44.0", {"start": v(8.8, -23.83) * mm, "mid": v(8.54, -23.58) * mm, "end": v(8.28, -23.34) * mm});
            skLineSegment(sketch, "E8.3.45.0", {"start": v(10.1, -22.62) * mm, "end": v(9.76, -22.76) * mm});
            skArc(sketch, "E8.6.45.0", {"start": v(9.72, -23.47) * mm, "mid": v(9.73, -23.11) * mm, "end": v(9.76, -22.76) * mm});
            skLineSegment(sketch, "E8.7.45.0", {"start": v(9.72, -23.47) * mm, "end": v(9.96, -24.05) * mm});
            skLineSegment(sketch, "E8.10.45.0", {"start": v(10.63, -23.07) * mm, "end": v(10.9, -23.64) * mm});
            skArc(sketch, "E8.13.45.0", {"start": v(10.63, -23.07) * mm, "mid": v(10.37, -22.84) * mm, "end": v(10.1, -22.62) * mm});
            skArc(sketch, "E8.17.45.0", {"start": v(10.63, -23.07) * mm, "mid": v(10.37, -22.84) * mm, "end": v(10.1, -22.62) * mm});
            skLineSegment(sketch, "E8.3.46.0", {"start": v(11.83, -21.76) * mm, "end": v(11.52, -21.93) * mm});
            skArc(sketch, "E8.6.46.0", {"start": v(11.53, -22.63) * mm, "mid": v(11.51, -22.28) * mm, "end": v(11.52, -21.93) * mm});
            skLineSegment(sketch, "E8.7.46.0", {"start": v(11.53, -22.63) * mm, "end": v(11.82, -23.2) * mm});
            skLineSegment(sketch, "E8.10.46.0", {"start": v(12.41, -22.16) * mm, "end": v(12.72, -22.72) * mm});
            skArc(sketch, "E8.13.46.0", {"start": v(12.41, -22.16) * mm, "mid": v(12.13, -21.95) * mm, "end": v(11.83, -21.76) * mm});
            skArc(sketch, "E8.17.46.0", {"start": v(12.41, -22.16) * mm, "mid": v(12.13, -21.95) * mm, "end": v(11.83, -21.76) * mm});
            skLineSegment(sketch, "E8.3.47.0", {"start": v(13.5, -20.76) * mm, "end": v(13.2, -20.96) * mm});
            skArc(sketch, "E8.6.47.0", {"start": v(13.27, -21.66) * mm, "mid": v(13.23, -21.3) * mm, "end": v(13.2, -20.96) * mm});
            skLineSegment(sketch, "E8.7.47.0", {"start": v(13.27, -21.66) * mm, "end": v(13.6, -22.2) * mm});
            skLineSegment(sketch, "E8.10.47.0", {"start": v(14.11, -21.12) * mm, "end": v(14.46, -21.65) * mm});
            skArc(sketch, "E8.13.47.0", {"start": v(14.11, -21.12) * mm, "mid": v(13.81, -20.93) * mm, "end": v(13.5, -20.76) * mm});
            skArc(sketch, "E8.17.47.0", {"start": v(14.11, -21.12) * mm, "mid": v(13.81, -20.93) * mm, "end": v(13.5, -20.76) * mm});
            skLineSegment(sketch, "E8.3.48.0", {"start": v(15.1, -19.64) * mm, "end": v(14.8, -19.86) * mm});
            skArc(sketch, "E8.6.48.0", {"start": v(14.93, -20.55) * mm, "mid": v(14.86, -20.2) * mm, "end": v(14.8, -19.86) * mm});
            skLineSegment(sketch, "E8.7.48.0", {"start": v(14.93, -20.55) * mm, "end": v(15.3, -21.06) * mm});
            skLineSegment(sketch, "E8.10.48.0", {"start": v(15.72, -19.95) * mm, "end": v(16.12, -20.45) * mm});
            skArc(sketch, "E8.13.48.0", {"start": v(15.72, -19.95) * mm, "mid": v(15.41, -19.78) * mm, "end": v(15.1, -19.64) * mm});
            skArc(sketch, "E8.17.48.0", {"start": v(15.72, -19.95) * mm, "mid": v(15.41, -19.78) * mm, "end": v(15.1, -19.64) * mm});
            skLineSegment(sketch, "E8.3.49.0", {"start": v(16.59, -18.4) * mm, "end": v(16.32, -18.63) * mm});
            skArc(sketch, "E8.6.49.0", {"start": v(16.5, -19.31) * mm, "mid": v(16.4, -18.98) * mm, "end": v(16.32, -18.63) * mm});
            skLineSegment(sketch, "E8.7.49.0", {"start": v(16.5, -19.31) * mm, "end": v(16.9, -19.8) * mm});
            skLineSegment(sketch, "E8.10.49.0", {"start": v(17.24, -18.65) * mm, "end": v(17.67, -19.12) * mm});
            skArc(sketch, "E8.13.49.0", {"start": v(17.24, -18.65) * mm, "mid": v(16.92, -18.51) * mm, "end": v(16.59, -18.4) * mm});
            skArc(sketch, "E8.17.49.0", {"start": v(17.24, -18.65) * mm, "mid": v(16.92, -18.51) * mm, "end": v(16.59, -18.4) * mm});
            skLineSegment(sketch, "E8.3.50.0", {"start": v(17.98, -17.04) * mm, "end": v(17.73, -17.3) * mm});
            skArc(sketch, "E8.6.50.0", {"start": v(17.96, -17.96) * mm, "mid": v(17.84, -17.63) * mm, "end": v(17.73, -17.3) * mm});
            skLineSegment(sketch, "E8.7.50.0", {"start": v(17.96, -17.96) * mm, "end": v(18.4, -18.4) * mm});
            skLineSegment(sketch, "E8.10.50.0", {"start": v(18.65, -17.24) * mm, "end": v(19.12, -17.67) * mm});
            skArc(sketch, "E8.13.50.0", {"start": v(18.65, -17.24) * mm, "mid": v(18.32, -17.13) * mm, "end": v(17.98, -17.04) * mm});
            skArc(sketch, "E8.17.50.0", {"start": v(18.65, -17.24) * mm, "mid": v(18.32, -17.13) * mm, "end": v(17.98, -17.04) * mm});
            skLineSegment(sketch, "E8.3.51.0", {"start": v(19.26, -15.57) * mm, "end": v(19.03, -15.85) * mm});
            skArc(sketch, "E8.6.51.0", {"start": v(19.31, -16.5) * mm, "mid": v(19.16, -16.18) * mm, "end": v(19.03, -15.85) * mm});
            skLineSegment(sketch, "E8.7.51.0", {"start": v(19.31, -16.5) * mm, "end": v(19.8, -16.9) * mm});
            skLineSegment(sketch, "E8.10.51.0", {"start": v(19.95, -15.72) * mm, "end": v(20.45, -16.12) * mm});
            skArc(sketch, "E8.13.51.0", {"start": v(19.95, -15.72) * mm, "mid": v(19.6, -15.64) * mm, "end": v(19.26, -15.57) * mm});
            skArc(sketch, "E8.17.51.0", {"start": v(19.95, -15.72) * mm, "mid": v(19.6, -15.64) * mm, "end": v(19.26, -15.57) * mm});
            skLineSegment(sketch, "E8.3.52.0", {"start": v(20.42, -14.01) * mm, "end": v(20.22, -14.3) * mm});
            skArc(sketch, "E8.6.52.0", {"start": v(20.55, -14.93) * mm, "mid": v(20.37, -14.62) * mm, "end": v(20.22, -14.3) * mm});
            skLineSegment(sketch, "E8.7.52.0", {"start": v(20.55, -14.93) * mm, "end": v(21.06, -15.3) * mm});
            skLineSegment(sketch, "E8.10.52.0", {"start": v(21.12, -14.11) * mm, "end": v(21.65, -14.46) * mm});
            skArc(sketch, "E8.13.52.0", {"start": v(21.12, -14.11) * mm, "mid": v(20.77, -14.05) * mm, "end": v(20.42, -14.01) * mm});
            skArc(sketch, "E8.17.52.0", {"start": v(21.12, -14.11) * mm, "mid": v(20.77, -14.05) * mm, "end": v(20.42, -14.01) * mm});
            skLineSegment(sketch, "E8.3.53.0", {"start": v(21.46, -12.37) * mm, "end": v(21.28, -12.68) * mm});
            skArc(sketch, "E8.6.53.0", {"start": v(21.66, -13.27) * mm, "mid": v(21.46, -12.98) * mm, "end": v(21.28, -12.68) * mm});
            skLineSegment(sketch, "E8.7.53.0", {"start": v(21.66, -13.27) * mm, "end": v(22.2, -13.6) * mm});
            skLineSegment(sketch, "E8.10.53.0", {"start": v(22.16, -12.41) * mm, "end": v(22.72, -12.72) * mm});
            skArc(sketch, "E8.13.53.0", {"start": v(22.16, -12.41) * mm, "mid": v(21.81, -12.38) * mm, "end": v(21.46, -12.37) * mm});
            skArc(sketch, "E8.17.53.0", {"start": v(22.16, -12.41) * mm, "mid": v(21.81, -12.38) * mm, "end": v(21.46, -12.37) * mm});
            skLineSegment(sketch, "E8.3.54.0", {"start": v(22.36, -10.65) * mm, "end": v(22.2, -10.97) * mm});
            skArc(sketch, "E8.6.54.0", {"start": v(22.63, -11.53) * mm, "mid": v(22.41, -11.26) * mm, "end": v(22.2, -10.97) * mm});
            skLineSegment(sketch, "E8.7.54.0", {"start": v(22.63, -11.53) * mm, "end": v(23.2, -11.82) * mm});
            skLineSegment(sketch, "E8.10.54.0", {"start": v(23.07, -10.63) * mm, "end": v(23.64, -10.9) * mm});
            skArc(sketch, "E8.13.54.0", {"start": v(23.07, -10.63) * mm, "mid": v(22.72, -10.63) * mm, "end": v(22.36, -10.65) * mm});
            skArc(sketch, "E8.17.54.0", {"start": v(23.07, -10.63) * mm, "mid": v(22.72, -10.63) * mm, "end": v(22.36, -10.65) * mm});
            skLineSegment(sketch, "E8.3.55.0", {"start": v(23.13, -8.86) * mm, "end": v(23, -9.2) * mm});
            skArc(sketch, "E8.6.55.0", {"start": v(23.47, -9.72) * mm, "mid": v(23.23, -9.46) * mm, "end": v(23, -9.2) * mm});
            skLineSegment(sketch, "E8.7.55.0", {"start": v(23.47, -9.72) * mm, "end": v(24.05, -9.96) * mm});
            skLineSegment(sketch, "E8.10.55.0", {"start": v(23.83, -8.8) * mm, "end": v(24.43, -9.01) * mm});
            skArc(sketch, "E8.13.55.0", {"start": v(23.83, -8.8) * mm, "mid": v(23.48, -8.82) * mm, "end": v(23.13, -8.86) * mm});
            skArc(sketch, "E8.17.55.0", {"start": v(23.83, -8.8) * mm, "mid": v(23.48, -8.82) * mm, "end": v(23.13, -8.86) * mm});
            skLineSegment(sketch, "E8.3.56.0", {"start": v(23.75, -7.02) * mm, "end": v(23.65, -7.36) * mm});
            skArc(sketch, "E8.6.56.0", {"start": v(24.16, -7.85) * mm, "mid": v(23.9, -7.61) * mm, "end": v(23.65, -7.36) * mm});
            skLineSegment(sketch, "E8.7.56.0", {"start": v(24.16, -7.85) * mm, "end": v(24.76, -8.05) * mm});
            skLineSegment(sketch, "E8.10.56.0", {"start": v(24.45, -6.9) * mm, "end": v(25.06, -7.07) * mm});
            skArc(sketch, "E8.13.56.0", {"start": v(24.45, -6.9) * mm, "mid": v(24.1, -6.95) * mm, "end": v(23.75, -7.02) * mm});
            skArc(sketch, "E8.17.56.0", {"start": v(24.45, -6.9) * mm, "mid": v(24.1, -6.95) * mm, "end": v(23.75, -7.02) * mm});
            skLineSegment(sketch, "E8.3.57.0", {"start": v(24.23, -5.13) * mm, "end": v(24.15, -5.48) * mm});
            skArc(sketch, "E8.6.57.0", {"start": v(24.7, -5.93) * mm, "mid": v(24.42, -5.71) * mm, "end": v(24.15, -5.48) * mm});
            skLineSegment(sketch, "E8.7.57.0", {"start": v(24.7, -5.93) * mm, "end": v(25.32, -6.08) * mm});
            skLineSegment(sketch, "E8.10.57.0", {"start": v(24.91, -4.96) * mm, "end": v(25.53, -5.08) * mm});
            skArc(sketch, "E8.13.57.0", {"start": v(24.91, -4.96) * mm, "mid": v(24.57, -5.03) * mm, "end": v(24.23, -5.13) * mm});
            skArc(sketch, "E8.17.57.0", {"start": v(24.91, -4.96) * mm, "mid": v(24.57, -5.03) * mm, "end": v(24.23, -5.13) * mm});
            skLineSegment(sketch, "E8.3.58.0", {"start": v(24.56, -3.22) * mm, "end": v(24.5, -3.57) * mm});
            skArc(sketch, "E8.6.58.0", {"start": v(25.09, -3.97) * mm, "mid": v(24.8, -3.78) * mm, "end": v(24.5, -3.57) * mm});
            skLineSegment(sketch, "E8.7.58.0", {"start": v(25.09, -3.97) * mm, "end": v(25.71, -4.07) * mm});
            skLineSegment(sketch, "E8.10.58.0", {"start": v(25.22, -2.99) * mm, "end": v(25.85, -3.06) * mm});
            skArc(sketch, "E8.13.58.0", {"start": v(25.22, -2.99) * mm, "mid": v(24.89, -3.1) * mm, "end": v(24.56, -3.22) * mm});
            skArc(sketch, "E8.17.58.0", {"start": v(25.22, -2.99) * mm, "mid": v(24.89, -3.1) * mm, "end": v(24.56, -3.22) * mm});
            skLineSegment(sketch, "E8.3.59.0", {"start": v(24.74, -1.28) * mm, "end": v(24.71, -1.64) * mm});
            skArc(sketch, "E8.6.59.0", {"start": v(25.32, -2) * mm, "mid": v(25.01, -1.82) * mm, "end": v(24.71, -1.64) * mm});
            skLineSegment(sketch, "E8.7.59.0", {"start": v(25.32, -2) * mm, "end": v(25.95, -2.04) * mm});
            skLineSegment(sketch, "E8.10.59.0", {"start": v(25.38, -1) * mm, "end": v(26.01, -1.02) * mm});
            skArc(sketch, "E8.13.59.0", {"start": v(25.38, -1) * mm, "mid": v(25.05, -1.13) * mm, "end": v(24.74, -1.28) * mm});
            skArc(sketch, "E8.17.59.0", {"start": v(25.38, -1) * mm, "mid": v(25.05, -1.13) * mm, "end": v(24.74, -1.28) * mm});
            skLineSegment(sketch, "E8.3.60.0", {"start": v(24.76, 0.67) * mm, "end": v(24.77, 0.3) * mm});
            skArc(sketch, "E8.6.60.0", {"start": v(25.4, 0) * mm, "mid": v(25.08, 0.14) * mm, "end": v(24.77, 0.3) * mm});
            skLineSegment(sketch, "E8.7.60.0", {"start": v(25.4, 0) * mm, "end": v(26.04, 0) * mm});
            skLineSegment(sketch, "E8.10.60.0", {"start": v(25.38, 1) * mm, "end": v(26.01, 1.02) * mm});
            skArc(sketch, "E8.13.60.0", {"start": v(25.38, 1) * mm, "mid": v(25.07, 0.84) * mm, "end": v(24.76, 0.67) * mm});
            skArc(sketch, "E8.17.60.0", {"start": v(25.38, 1) * mm, "mid": v(25.07, 0.84) * mm, "end": v(24.76, 0.67) * mm});
            skLineSegment(sketch, "E8.3.61.0", {"start": v(24.63, 2.6) * mm, "end": v(24.67, 2.25) * mm});
            skArc(sketch, "E8.6.61.0", {"start": v(25.32, 2) * mm, "mid": v(25, 2.11) * mm, "end": v(24.67, 2.25) * mm});
            skLineSegment(sketch, "E8.7.61.0", {"start": v(25.32, 2) * mm, "end": v(25.95, 2.04) * mm});
            skLineSegment(sketch, "E8.10.61.0", {"start": v(25.22, 2.99) * mm, "end": v(25.85, 3.06) * mm});
            skArc(sketch, "E8.13.61.0", {"start": v(25.22, 2.99) * mm, "mid": v(24.92, 2.8) * mm, "end": v(24.63, 2.6) * mm});
            skArc(sketch, "E8.17.61.0", {"start": v(25.22, 2.99) * mm, "mid": v(24.92, 2.8) * mm, "end": v(24.63, 2.6) * mm});
            skLineSegment(sketch, "E8.3.62.0", {"start": v(24.35, 4.53) * mm, "end": v(24.41, 4.18) * mm});
            skArc(sketch, "E8.6.62.0", {"start": v(25.09, 3.97) * mm, "mid": v(24.75, 4.07) * mm, "end": v(24.41, 4.18) * mm});
            skLineSegment(sketch, "E8.7.62.0", {"start": v(25.09, 3.97) * mm, "end": v(25.71, 4.07) * mm});
            skLineSegment(sketch, "E8.10.62.0", {"start": v(24.91, 4.96) * mm, "end": v(25.53, 5.08) * mm});
            skArc(sketch, "E8.13.62.0", {"start": v(24.91, 4.96) * mm, "mid": v(24.63, 4.75) * mm, "end": v(24.35, 4.53) * mm});
            skArc(sketch, "E8.17.62.0", {"start": v(24.91, 4.96) * mm, "mid": v(24.63, 4.75) * mm, "end": v(24.35, 4.53) * mm});
            skLineSegment(sketch, "E8.3.63.0", {"start": v(23.92, 6.43) * mm, "end": v(24.01, 6.08) * mm});
            skArc(sketch, "E8.6.63.0", {"start": v(24.7, 5.93) * mm, "mid": v(24.35, 6) * mm, "end": v(24.01, 6.08) * mm});
            skLineSegment(sketch, "E8.7.63.0", {"start": v(24.7, 5.93) * mm, "end": v(25.32, 6.08) * mm});
            skLineSegment(sketch, "E8.10.63.0", {"start": v(24.45, 6.9) * mm, "end": v(25.06, 7.07) * mm});
            skArc(sketch, "E8.13.63.0", {"start": v(24.45, 6.9) * mm, "mid": v(24.18, 6.67) * mm, "end": v(23.92, 6.43) * mm});
            skArc(sketch, "E8.17.63.0", {"start": v(24.45, 6.9) * mm, "mid": v(24.18, 6.67) * mm, "end": v(23.92, 6.43) * mm});
            skLineSegment(sketch, "E8.3.64.0", {"start": v(23.34, 8.28) * mm, "end": v(23.46, 7.94) * mm});
            skArc(sketch, "E8.6.64.0", {"start": v(24.16, 7.85) * mm, "mid": v(23.8, 7.89) * mm, "end": v(23.46, 7.94) * mm});
            skLineSegment(sketch, "E8.7.64.0", {"start": v(24.16, 7.85) * mm, "end": v(24.76, 8.05) * mm});
            skLineSegment(sketch, "E8.10.64.0", {"start": v(23.83, 8.8) * mm, "end": v(24.43, 9.01) * mm});
            skArc(sketch, "E8.13.64.0", {"start": v(23.83, 8.8) * mm, "mid": v(23.58, 8.54) * mm, "end": v(23.34, 8.28) * mm});
            skArc(sketch, "E8.17.64.0", {"start": v(23.83, 8.8) * mm, "mid": v(23.58, 8.54) * mm, "end": v(23.34, 8.28) * mm});
            skLineSegment(sketch, "E8.3.65.0", {"start": v(22.62, 10.1) * mm, "end": v(22.76, 9.76) * mm});
            skArc(sketch, "E8.6.65.0", {"start": v(23.47, 9.72) * mm, "mid": v(23.11, 9.73) * mm, "end": v(22.76, 9.76) * mm});
            skLineSegment(sketch, "E8.7.65.0", {"start": v(23.47, 9.72) * mm, "end": v(24.05, 9.96) * mm});
            skLineSegment(sketch, "E8.10.65.0", {"start": v(23.07, 10.63) * mm, "end": v(23.64, 10.9) * mm});
            skArc(sketch, "E8.13.65.0", {"start": v(23.07, 10.63) * mm, "mid": v(22.84, 10.37) * mm, "end": v(22.62, 10.1) * mm});
            skArc(sketch, "E8.17.65.0", {"start": v(23.07, 10.63) * mm, "mid": v(22.84, 10.37) * mm, "end": v(22.62, 10.1) * mm});
            skLineSegment(sketch, "E8.3.66.0", {"start": v(21.76, 11.83) * mm, "end": v(21.93, 11.52) * mm});
            skArc(sketch, "E8.6.66.0", {"start": v(22.63, 11.53) * mm, "mid": v(22.28, 11.51) * mm, "end": v(21.93, 11.52) * mm});
            skLineSegment(sketch, "E8.7.66.0", {"start": v(22.63, 11.53) * mm, "end": v(23.2, 11.82) * mm});
            skLineSegment(sketch, "E8.10.66.0", {"start": v(22.16, 12.41) * mm, "end": v(22.72, 12.72) * mm});
            skArc(sketch, "E8.13.66.0", {"start": v(22.16, 12.41) * mm, "mid": v(21.95, 12.13) * mm, "end": v(21.76, 11.83) * mm});
            skArc(sketch, "E8.17.66.0", {"start": v(22.16, 12.41) * mm, "mid": v(21.95, 12.13) * mm, "end": v(21.76, 11.83) * mm});
            skLineSegment(sketch, "E8.3.67.0", {"start": v(20.76, 13.5) * mm, "end": v(20.96, 13.2) * mm});
            skArc(sketch, "E8.6.67.0", {"start": v(21.66, 13.27) * mm, "mid": v(21.3, 13.23) * mm, "end": v(20.96, 13.2) * mm});
            skLineSegment(sketch, "E8.7.67.0", {"start": v(21.66, 13.27) * mm, "end": v(22.2, 13.6) * mm});
            skLineSegment(sketch, "E8.10.67.0", {"start": v(21.12, 14.11) * mm, "end": v(21.65, 14.46) * mm});
            skArc(sketch, "E8.13.67.0", {"start": v(21.12, 14.11) * mm, "mid": v(20.93, 13.81) * mm, "end": v(20.76, 13.5) * mm});
            skArc(sketch, "E8.17.67.0", {"start": v(21.12, 14.11) * mm, "mid": v(20.93, 13.81) * mm, "end": v(20.76, 13.5) * mm});
            skLineSegment(sketch, "E8.3.68.0", {"start": v(19.64, 15.1) * mm, "end": v(19.86, 14.8) * mm});
            skArc(sketch, "E8.6.68.0", {"start": v(20.55, 14.93) * mm, "mid": v(20.2, 14.86) * mm, "end": v(19.86, 14.8) * mm});
            skLineSegment(sketch, "E8.7.68.0", {"start": v(20.55, 14.93) * mm, "end": v(21.06, 15.3) * mm});
            skLineSegment(sketch, "E8.10.68.0", {"start": v(19.95, 15.72) * mm, "end": v(20.45, 16.12) * mm});
            skArc(sketch, "E8.13.68.0", {"start": v(19.95, 15.72) * mm, "mid": v(19.78, 15.41) * mm, "end": v(19.64, 15.1) * mm});
            skArc(sketch, "E8.17.68.0", {"start": v(19.95, 15.72) * mm, "mid": v(19.78, 15.41) * mm, "end": v(19.64, 15.1) * mm});
            skLineSegment(sketch, "E8.3.69.0", {"start": v(18.4, 16.59) * mm, "end": v(18.63, 16.32) * mm});
            skArc(sketch, "E8.6.69.0", {"start": v(19.31, 16.5) * mm, "mid": v(18.98, 16.4) * mm, "end": v(18.63, 16.32) * mm});
            skLineSegment(sketch, "E8.7.69.0", {"start": v(19.31, 16.5) * mm, "end": v(19.8, 16.9) * mm});
            skLineSegment(sketch, "E8.10.69.0", {"start": v(18.65, 17.24) * mm, "end": v(19.12, 17.67) * mm});
            skArc(sketch, "E8.13.69.0", {"start": v(18.65, 17.24) * mm, "mid": v(18.51, 16.92) * mm, "end": v(18.4, 16.59) * mm});
            skArc(sketch, "E8.17.69.0", {"start": v(18.65, 17.24) * mm, "mid": v(18.51, 16.92) * mm, "end": v(18.4, 16.59) * mm});
            skLineSegment(sketch, "E8.3.70.0", {"start": v(17.04, 17.98) * mm, "end": v(17.3, 17.73) * mm});
            skArc(sketch, "E8.6.70.0", {"start": v(17.96, 17.96) * mm, "mid": v(17.63, 17.84) * mm, "end": v(17.3, 17.73) * mm});
            skLineSegment(sketch, "E8.7.70.0", {"start": v(17.96, 17.96) * mm, "end": v(18.4, 18.4) * mm});
            skLineSegment(sketch, "E8.10.70.0", {"start": v(17.24, 18.65) * mm, "end": v(17.67, 19.12) * mm});
            skArc(sketch, "E8.13.70.0", {"start": v(17.24, 18.65) * mm, "mid": v(17.13, 18.32) * mm, "end": v(17.04, 17.98) * mm});
            skArc(sketch, "E8.17.70.0", {"start": v(17.24, 18.65) * mm, "mid": v(17.13, 18.32) * mm, "end": v(17.04, 17.98) * mm});
            skLineSegment(sketch, "E8.3.71.0", {"start": v(15.57, 19.26) * mm, "end": v(15.85, 19.03) * mm});
            skArc(sketch, "E8.6.71.0", {"start": v(16.5, 19.31) * mm, "mid": v(16.18, 19.16) * mm, "end": v(15.85, 19.03) * mm});
            skLineSegment(sketch, "E8.7.71.0", {"start": v(16.5, 19.31) * mm, "end": v(16.9, 19.8) * mm});
            skLineSegment(sketch, "E8.10.71.0", {"start": v(15.72, 19.95) * mm, "end": v(16.12, 20.45) * mm});
            skArc(sketch, "E8.13.71.0", {"start": v(15.72, 19.95) * mm, "mid": v(15.64, 19.6) * mm, "end": v(15.57, 19.26) * mm});
            skArc(sketch, "E8.17.71.0", {"start": v(15.72, 19.95) * mm, "mid": v(15.64, 19.6) * mm, "end": v(15.57, 19.26) * mm});
            skLineSegment(sketch, "E8.3.72.0", {"start": v(14.01, 20.42) * mm, "end": v(14.3, 20.22) * mm});
            skArc(sketch, "E8.6.72.0", {"start": v(14.93, 20.55) * mm, "mid": v(14.62, 20.37) * mm, "end": v(14.3, 20.22) * mm});
            skLineSegment(sketch, "E8.7.72.0", {"start": v(14.93, 20.55) * mm, "end": v(15.3, 21.06) * mm});
            skLineSegment(sketch, "E8.10.72.0", {"start": v(14.11, 21.12) * mm, "end": v(14.46, 21.65) * mm});
            skArc(sketch, "E8.13.72.0", {"start": v(14.11, 21.12) * mm, "mid": v(14.05, 20.77) * mm, "end": v(14.01, 20.42) * mm});
            skArc(sketch, "E8.17.72.0", {"start": v(14.11, 21.12) * mm, "mid": v(14.05, 20.77) * mm, "end": v(14.01, 20.42) * mm});
            skLineSegment(sketch, "E8.3.73.0", {"start": v(12.37, 21.46) * mm, "end": v(12.68, 21.28) * mm});
            skArc(sketch, "E8.6.73.0", {"start": v(13.27, 21.66) * mm, "mid": v(12.98, 21.46) * mm, "end": v(12.68, 21.28) * mm});
            skLineSegment(sketch, "E8.7.73.0", {"start": v(13.27, 21.66) * mm, "end": v(13.6, 22.2) * mm});
            skLineSegment(sketch, "E8.10.73.0", {"start": v(12.41, 22.16) * mm, "end": v(12.72, 22.72) * mm});
            skArc(sketch, "E8.13.73.0", {"start": v(12.41, 22.16) * mm, "mid": v(12.38, 21.81) * mm, "end": v(12.37, 21.46) * mm});
            skArc(sketch, "E8.17.73.0", {"start": v(12.41, 22.16) * mm, "mid": v(12.38, 21.81) * mm, "end": v(12.37, 21.46) * mm});
            skLineSegment(sketch, "E8.3.74.0", {"start": v(10.65, 22.36) * mm, "end": v(10.97, 22.2) * mm});
            skArc(sketch, "E8.6.74.0", {"start": v(11.53, 22.63) * mm, "mid": v(11.26, 22.41) * mm, "end": v(10.97, 22.2) * mm});
            skLineSegment(sketch, "E8.7.74.0", {"start": v(11.53, 22.63) * mm, "end": v(11.82, 23.2) * mm});
            skLineSegment(sketch, "E8.10.74.0", {"start": v(10.63, 23.07) * mm, "end": v(10.9, 23.64) * mm});
            skArc(sketch, "E8.13.74.0", {"start": v(10.63, 23.07) * mm, "mid": v(10.63, 22.72) * mm, "end": v(10.65, 22.36) * mm});
            skArc(sketch, "E8.17.74.0", {"start": v(10.63, 23.07) * mm, "mid": v(10.63, 22.72) * mm, "end": v(10.65, 22.36) * mm});
            skLineSegment(sketch, "E8.3.75.0", {"start": v(8.86, 23.13) * mm, "end": v(9.2, 23) * mm});
            skArc(sketch, "E8.6.75.0", {"start": v(9.72, 23.47) * mm, "mid": v(9.46, 23.23) * mm, "end": v(9.2, 23) * mm});
            skLineSegment(sketch, "E8.7.75.0", {"start": v(9.72, 23.47) * mm, "end": v(9.96, 24.05) * mm});
            skLineSegment(sketch, "E8.10.75.0", {"start": v(8.8, 23.83) * mm, "end": v(9.01, 24.43) * mm});
            skArc(sketch, "E8.13.75.0", {"start": v(8.8, 23.83) * mm, "mid": v(8.82, 23.48) * mm, "end": v(8.86, 23.13) * mm});
            skArc(sketch, "E8.17.75.0", {"start": v(8.8, 23.83) * mm, "mid": v(8.82, 23.48) * mm, "end": v(8.86, 23.13) * mm});
            skLineSegment(sketch, "E8.3.76.0", {"start": v(7.02, 23.75) * mm, "end": v(7.36, 23.65) * mm});
            skArc(sketch, "E8.6.76.0", {"start": v(7.85, 24.16) * mm, "mid": v(7.61, 23.9) * mm, "end": v(7.36, 23.65) * mm});
            skLineSegment(sketch, "E8.7.76.0", {"start": v(7.85, 24.16) * mm, "end": v(8.05, 24.76) * mm});
            skLineSegment(sketch, "E8.10.76.0", {"start": v(6.9, 24.45) * mm, "end": v(7.07, 25.06) * mm});
            skArc(sketch, "E8.13.76.0", {"start": v(6.9, 24.45) * mm, "mid": v(6.95, 24.1) * mm, "end": v(7.02, 23.75) * mm});
            skArc(sketch, "E8.17.76.0", {"start": v(6.9, 24.45) * mm, "mid": v(6.95, 24.1) * mm, "end": v(7.02, 23.75) * mm});
            skLineSegment(sketch, "E8.3.77.0", {"start": v(5.13, 24.23) * mm, "end": v(5.48, 24.15) * mm});
            skArc(sketch, "E8.6.77.0", {"start": v(5.93, 24.7) * mm, "mid": v(5.71, 24.42) * mm, "end": v(5.48, 24.15) * mm});
            skLineSegment(sketch, "E8.7.77.0", {"start": v(5.93, 24.7) * mm, "end": v(6.08, 25.32) * mm});
            skLineSegment(sketch, "E8.10.77.0", {"start": v(4.96, 24.91) * mm, "end": v(5.08, 25.53) * mm});
            skArc(sketch, "E8.13.77.0", {"start": v(4.96, 24.91) * mm, "mid": v(5.03, 24.57) * mm, "end": v(5.13, 24.23) * mm});
            skArc(sketch, "E8.17.77.0", {"start": v(4.96, 24.91) * mm, "mid": v(5.03, 24.57) * mm, "end": v(5.13, 24.23) * mm});
            skLineSegment(sketch, "E8.3.78.0", {"start": v(3.22, 24.56) * mm, "end": v(3.57, 24.5) * mm});
            skArc(sketch, "E8.6.78.0", {"start": v(3.97, 25.09) * mm, "mid": v(3.78, 24.8) * mm, "end": v(3.57, 24.5) * mm});
            skLineSegment(sketch, "E8.7.78.0", {"start": v(3.97, 25.09) * mm, "end": v(4.07, 25.71) * mm});
            skLineSegment(sketch, "E8.10.78.0", {"start": v(2.99, 25.22) * mm, "end": v(3.06, 25.85) * mm});
            skArc(sketch, "E8.13.78.0", {"start": v(2.99, 25.22) * mm, "mid": v(3.1, 24.89) * mm, "end": v(3.22, 24.56) * mm});
            skArc(sketch, "E8.17.78.0", {"start": v(2.99, 25.22) * mm, "mid": v(3.1, 24.89) * mm, "end": v(3.22, 24.56) * mm});
            skLineSegment(sketch, "E8.3.79.0", {"start": v(1.28, 24.74) * mm, "end": v(1.64, 24.71) * mm});
            skArc(sketch, "E8.6.79.0", {"start": v(2, 25.32) * mm, "mid": v(1.82, 25.01) * mm, "end": v(1.64, 24.71) * mm});
            skLineSegment(sketch, "E8.7.79.0", {"start": v(2, 25.32) * mm, "end": v(2.04, 25.95) * mm});
            skLineSegment(sketch, "E8.10.79.0", {"start": v(1, 25.38) * mm, "end": v(1.02, 26.01) * mm});
            skArc(sketch, "E8.13.79.0", {"start": v(1, 25.38) * mm, "mid": v(1.13, 25.05) * mm, "end": v(1.28, 24.74) * mm});
            skArc(sketch, "E8.17.79.0", {"start": v(1, 25.38) * mm, "mid": v(1.13, 25.05) * mm, "end": v(1.28, 24.74) * mm});
            skArc(sketch, "E9.1.0", {"start": v(-3.06, 25.85) * mm, "mid": v(-3.57, 25.79) * mm, "end": v(-4.07, 25.71) * mm});
            skArc(sketch, "E9.2.0", {"start": v(-5.08, 25.53) * mm, "mid": v(-5.58, 25.43) * mm, "end": v(-6.08, 25.32) * mm});
            skArc(sketch, "E10.3.3.0", {"start": v(-7.07, 25.06) * mm, "mid": v(-7.56, 24.91) * mm, "end": v(-8.05, 24.76) * mm});
            skArc(sketch, "E10.3.4.0", {"start": v(-9.01, 24.43) * mm, "mid": v(-9.49, 24.24) * mm, "end": v(-9.96, 24.05) * mm});
            skArc(sketch, "E10.3.5.0", {"start": v(-10.9, 23.64) * mm, "mid": v(-11.36, 23.42) * mm, "end": v(-11.82, 23.2) * mm});
            skArc(sketch, "E10.3.6.0", {"start": v(-12.72, 22.72) * mm, "mid": v(-13.16, 22.46) * mm, "end": v(-13.6, 22.2) * mm});
            skArc(sketch, "E10.3.7.0", {"start": v(-14.46, 21.65) * mm, "mid": v(-14.89, 21.36) * mm, "end": v(-15.3, 21.06) * mm});
            skArc(sketch, "E10.3.8.0", {"start": v(-16.12, 20.45) * mm, "mid": v(-16.52, 20.13) * mm, "end": v(-16.9, 19.8) * mm});
            skArc(sketch, "E10.3.9.0", {"start": v(-17.67, 19.12) * mm, "mid": v(-18.04, 18.77) * mm, "end": v(-18.4, 18.4) * mm});
            skArc(sketch, "E10.3.10.0", {"start": v(-19.12, 17.67) * mm, "mid": v(-19.46, 17.3) * mm, "end": v(-19.8, 16.9) * mm});
            skArc(sketch, "E10.3.11.0", {"start": v(-20.45, 16.12) * mm, "mid": v(-20.76, 15.71) * mm, "end": v(-21.06, 15.3) * mm});
            skArc(sketch, "E10.3.12.0", {"start": v(-21.65, 14.46) * mm, "mid": v(-21.93, 14.04) * mm, "end": v(-22.2, 13.6) * mm});
            skArc(sketch, "E10.3.13.0", {"start": v(-22.72, 12.72) * mm, "mid": v(-22.96, 12.27) * mm, "end": v(-23.2, 11.82) * mm});
            skArc(sketch, "E10.3.14.0", {"start": v(-23.64, 10.9) * mm, "mid": v(-23.85, 10.43) * mm, "end": v(-24.05, 9.96) * mm});
            skArc(sketch, "E10.3.15.0", {"start": v(-24.43, 9.01) * mm, "mid": v(-24.6, 8.53) * mm, "end": v(-24.76, 8.05) * mm});
            skArc(sketch, "E10.3.16.0", {"start": v(-25.06, 7.07) * mm, "mid": v(-25.2, 6.57) * mm, "end": v(-25.32, 6.08) * mm});
            skArc(sketch, "E10.3.17.0", {"start": v(-25.53, 5.08) * mm, "mid": v(-25.63, 4.58) * mm, "end": v(-25.71, 4.07) * mm});
            skArc(sketch, "E10.3.18.0", {"start": v(-25.85, 3.06) * mm, "mid": v(-25.9, 2.55) * mm, "end": v(-25.95, 2.04) * mm});
            skArc(sketch, "E10.3.19.0", {"start": v(-26.01, 1.02) * mm, "mid": v(-26.03, 0.51) * mm, "end": v(-26.04, 0) * mm});
            skArc(sketch, "E10.3.20.0", {"start": v(-26.01, -1.02) * mm, "mid": v(-25.99, -1.53) * mm, "end": v(-25.95, -2.04) * mm});
            skArc(sketch, "E10.3.21.0", {"start": v(-25.85, -3.06) * mm, "mid": v(-25.79, -3.57) * mm, "end": v(-25.71, -4.07) * mm});
            skArc(sketch, "E10.3.22.0", {"start": v(-25.53, -5.08) * mm, "mid": v(-25.43, -5.58) * mm, "end": v(-25.32, -6.08) * mm});
            skArc(sketch, "E10.3.23.0", {"start": v(-25.06, -7.07) * mm, "mid": v(-24.91, -7.56) * mm, "end": v(-24.76, -8.05) * mm});
            skArc(sketch, "E10.3.24.0", {"start": v(-24.43, -9.01) * mm, "mid": v(-24.24, -9.49) * mm, "end": v(-24.05, -9.96) * mm});
            skArc(sketch, "E10.3.25.0", {"start": v(-23.64, -10.9) * mm, "mid": v(-23.42, -11.36) * mm, "end": v(-23.2, -11.82) * mm});
            skArc(sketch, "E10.3.26.0", {"start": v(-22.72, -12.72) * mm, "mid": v(-22.46, -13.16) * mm, "end": v(-22.2, -13.6) * mm});
            skArc(sketch, "E10.3.27.0", {"start": v(-21.65, -14.46) * mm, "mid": v(-21.36, -14.89) * mm, "end": v(-21.06, -15.3) * mm});
            skArc(sketch, "E10.3.28.0", {"start": v(-20.45, -16.12) * mm, "mid": v(-20.13, -16.52) * mm, "end": v(-19.8, -16.9) * mm});
            skArc(sketch, "E10.3.29.0", {"start": v(-19.12, -17.67) * mm, "mid": v(-18.77, -18.04) * mm, "end": v(-18.4, -18.4) * mm});
            skArc(sketch, "E10.3.30.0", {"start": v(-17.67, -19.12) * mm, "mid": v(-17.3, -19.46) * mm, "end": v(-16.9, -19.8) * mm});
            skArc(sketch, "E10.3.31.0", {"start": v(-16.12, -20.45) * mm, "mid": v(-15.71, -20.76) * mm, "end": v(-15.3, -21.06) * mm});
            skArc(sketch, "E10.3.32.0", {"start": v(-14.46, -21.65) * mm, "mid": v(-14.04, -21.93) * mm, "end": v(-13.6, -22.2) * mm});
            skArc(sketch, "E10.3.33.0", {"start": v(-12.72, -22.72) * mm, "mid": v(-12.27, -22.96) * mm, "end": v(-11.82, -23.2) * mm});
            skArc(sketch, "E10.3.34.0", {"start": v(-10.9, -23.64) * mm, "mid": v(-10.43, -23.85) * mm, "end": v(-9.96, -24.05) * mm});
            skArc(sketch, "E10.3.35.0", {"start": v(-9.01, -24.43) * mm, "mid": v(-8.53, -24.6) * mm, "end": v(-8.05, -24.76) * mm});
            skArc(sketch, "E10.3.36.0", {"start": v(-7.07, -25.06) * mm, "mid": v(-6.57, -25.2) * mm, "end": v(-6.08, -25.32) * mm});
            skArc(sketch, "E10.3.37.0", {"start": v(-5.08, -25.53) * mm, "mid": v(-4.58, -25.63) * mm, "end": v(-4.07, -25.71) * mm});
            skArc(sketch, "E10.3.38.0", {"start": v(-3.06, -25.85) * mm, "mid": v(-2.55, -25.9) * mm, "end": v(-2.04, -25.95) * mm});
            skArc(sketch, "E10.3.39.0", {"start": v(-1.02, -26.01) * mm, "mid": v(-0.51, -26.03) * mm, "end": v(0, -26.04) * mm});
            skArc(sketch, "E10.3.40.0", {"start": v(1.02, -26.01) * mm, "mid": v(1.53, -25.99) * mm, "end": v(2.04, -25.95) * mm});
            skArc(sketch, "E10.3.41.0", {"start": v(3.06, -25.85) * mm, "mid": v(3.57, -25.79) * mm, "end": v(4.07, -25.71) * mm});
            skArc(sketch, "E10.3.42.0", {"start": v(5.08, -25.53) * mm, "mid": v(5.58, -25.43) * mm, "end": v(6.08, -25.32) * mm});
            skArc(sketch, "E10.3.43.0", {"start": v(7.07, -25.06) * mm, "mid": v(7.56, -24.91) * mm, "end": v(8.05, -24.76) * mm});
            skArc(sketch, "E10.3.44.0", {"start": v(9.01, -24.43) * mm, "mid": v(9.49, -24.24) * mm, "end": v(9.96, -24.05) * mm});
            skArc(sketch, "E10.3.45.0", {"start": v(10.9, -23.64) * mm, "mid": v(11.36, -23.42) * mm, "end": v(11.82, -23.2) * mm});
            skArc(sketch, "E10.3.46.0", {"start": v(12.72, -22.72) * mm, "mid": v(13.16, -22.46) * mm, "end": v(13.6, -22.2) * mm});
            skArc(sketch, "E10.3.47.0", {"start": v(14.46, -21.65) * mm, "mid": v(14.89, -21.36) * mm, "end": v(15.3, -21.06) * mm});
            skArc(sketch, "E10.3.48.0", {"start": v(16.12, -20.45) * mm, "mid": v(16.52, -20.13) * mm, "end": v(16.9, -19.8) * mm});
            skArc(sketch, "E10.3.49.0", {"start": v(17.67, -19.12) * mm, "mid": v(18.04, -18.77) * mm, "end": v(18.4, -18.4) * mm});
            skArc(sketch, "E10.3.50.0", {"start": v(19.12, -17.67) * mm, "mid": v(19.46, -17.3) * mm, "end": v(19.8, -16.9) * mm});
            skArc(sketch, "E10.3.51.0", {"start": v(20.45, -16.12) * mm, "mid": v(20.76, -15.71) * mm, "end": v(21.06, -15.3) * mm});
            skArc(sketch, "E10.3.52.0", {"start": v(21.65, -14.46) * mm, "mid": v(21.93, -14.04) * mm, "end": v(22.2, -13.6) * mm});
            skArc(sketch, "E10.3.53.0", {"start": v(22.72, -12.72) * mm, "mid": v(22.96, -12.27) * mm, "end": v(23.2, -11.82) * mm});
            skArc(sketch, "E10.3.54.0", {"start": v(23.64, -10.9) * mm, "mid": v(23.85, -10.43) * mm, "end": v(24.05, -9.96) * mm});
            skArc(sketch, "E10.3.55.0", {"start": v(24.43, -9.01) * mm, "mid": v(24.6, -8.53) * mm, "end": v(24.76, -8.05) * mm});
            skArc(sketch, "E10.3.56.0", {"start": v(25.06, -7.07) * mm, "mid": v(25.2, -6.57) * mm, "end": v(25.32, -6.08) * mm});
            skArc(sketch, "E10.3.57.0", {"start": v(25.53, -5.08) * mm, "mid": v(25.63, -4.58) * mm, "end": v(25.71, -4.07) * mm});
            skArc(sketch, "E10.3.58.0", {"start": v(25.85, -3.06) * mm, "mid": v(25.9, -2.55) * mm, "end": v(25.95, -2.04) * mm});
            skArc(sketch, "E10.3.59.0", {"start": v(26.01, -1.02) * mm, "mid": v(26.03, -0.51) * mm, "end": v(26.04, 0) * mm});
            skArc(sketch, "E10.3.60.0", {"start": v(26.01, 1.02) * mm, "mid": v(25.99, 1.53) * mm, "end": v(25.95, 2.04) * mm});
            skArc(sketch, "E10.3.61.0", {"start": v(25.85, 3.06) * mm, "mid": v(25.79, 3.57) * mm, "end": v(25.71, 4.07) * mm});
            skArc(sketch, "E10.3.62.0", {"start": v(25.53, 5.08) * mm, "mid": v(25.43, 5.58) * mm, "end": v(25.32, 6.08) * mm});
            skArc(sketch, "E10.3.63.0", {"start": v(25.06, 7.07) * mm, "mid": v(24.91, 7.56) * mm, "end": v(24.76, 8.05) * mm});
            skArc(sketch, "E10.3.64.0", {"start": v(24.43, 9.01) * mm, "mid": v(24.24, 9.49) * mm, "end": v(24.05, 9.96) * mm});
            skArc(sketch, "E10.3.65.0", {"start": v(23.64, 10.9) * mm, "mid": v(23.42, 11.36) * mm, "end": v(23.2, 11.82) * mm});
            skArc(sketch, "E10.3.66.0", {"start": v(22.72, 12.72) * mm, "mid": v(22.46, 13.16) * mm, "end": v(22.2, 13.6) * mm});
            skArc(sketch, "E10.3.67.0", {"start": v(21.65, 14.46) * mm, "mid": v(21.36, 14.89) * mm, "end": v(21.06, 15.3) * mm});
            skArc(sketch, "E10.3.68.0", {"start": v(20.45, 16.12) * mm, "mid": v(20.13, 16.52) * mm, "end": v(19.8, 16.9) * mm});
            skArc(sketch, "E10.3.69.0", {"start": v(19.12, 17.67) * mm, "mid": v(18.77, 18.04) * mm, "end": v(18.4, 18.4) * mm});
            skArc(sketch, "E10.3.70.0", {"start": v(17.67, 19.12) * mm, "mid": v(17.3, 19.46) * mm, "end": v(16.9, 19.8) * mm});
            skArc(sketch, "E10.3.71.0", {"start": v(16.12, 20.45) * mm, "mid": v(15.71, 20.76) * mm, "end": v(15.3, 21.06) * mm});
            skArc(sketch, "E10.3.72.0", {"start": v(14.46, 21.65) * mm, "mid": v(14.04, 21.93) * mm, "end": v(13.6, 22.2) * mm});
            skArc(sketch, "E10.3.73.0", {"start": v(12.72, 22.72) * mm, "mid": v(12.27, 22.96) * mm, "end": v(11.82, 23.2) * mm});
            skArc(sketch, "E10.3.74.0", {"start": v(10.9, 23.64) * mm, "mid": v(10.43, 23.85) * mm, "end": v(9.96, 24.05) * mm});
            skArc(sketch, "E10.3.75.0", {"start": v(9.01, 24.43) * mm, "mid": v(8.53, 24.6) * mm, "end": v(8.05, 24.76) * mm});
            skArc(sketch, "E10.3.76.0", {"start": v(7.07, 25.06) * mm, "mid": v(6.57, 25.2) * mm, "end": v(6.08, 25.32) * mm});
            skArc(sketch, "E10.3.77.0", {"start": v(5.08, 25.53) * mm, "mid": v(4.58, 25.63) * mm, "end": v(4.07, 25.71) * mm});
            skArc(sketch, "E10.3.78.0", {"start": v(3.06, 25.85) * mm, "mid": v(2.55, 25.9) * mm, "end": v(2.04, 25.95) * mm});
            skArc(sketch, "E10.3.79.0", {"start": v(1.02, 26.01) * mm, "mid": v(0.51, 26.03) * mm, "end": v(0, 26.04) * mm});
            skSolve(sketch);
        }
        {
            var Q0;
            Q0 = qSketchRegion(id + "F0", true);
            extrude(context, id + "F1", {"entities" : qUnion([Q0]), "depth" : 6.35 * mm});
        }
    });
